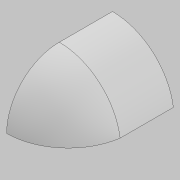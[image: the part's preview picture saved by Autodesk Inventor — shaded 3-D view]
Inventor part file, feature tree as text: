
AUTODESK INVENTOR PART (.ipt)
format: ipt  version: 2021 (Build 250183000, 183)  size: 132,608 bytes
history: native  units: mm
features: sketch x3, other x2, extrude x2, revolve x1
ambient origin geometry x8: Origin, YZ Plane, XZ Plane, XY Plane, X Axis, Y Axis, Z Axis, Center Point
bodies: Body1 (feature_tree)
feature tree (8):
  revolve  "Revolution2"  [1 undecoded]
  other  "end1"
  extrude  "Extrusion1"  Depth=150.0mm
  other  "end2"
  extrude  "Extrusion2"  Depth=10.0mm
  sketch  "Sketch1"  dims[d0=0.0mm d1=0.0mm]
  sketch  "Sketch3"  dims[d2=0.0mm d3=150.0mm]
  sketch  "Sketch4"  dims[d6=890.0mm d8=1029.125843mm d10=0.0mm d11=10.0mm d12=0.0mm d13=90.0deg d14=1029.125843mm d15=0.0mm d16=900.0mm d17=0.0mm d9=0.872665mm]
note: 1 required parameter value undecoded (feature->parameter linkage not recoverable at this tier; creation-order binding heuristic only, values carry confidence <= 0.55)
